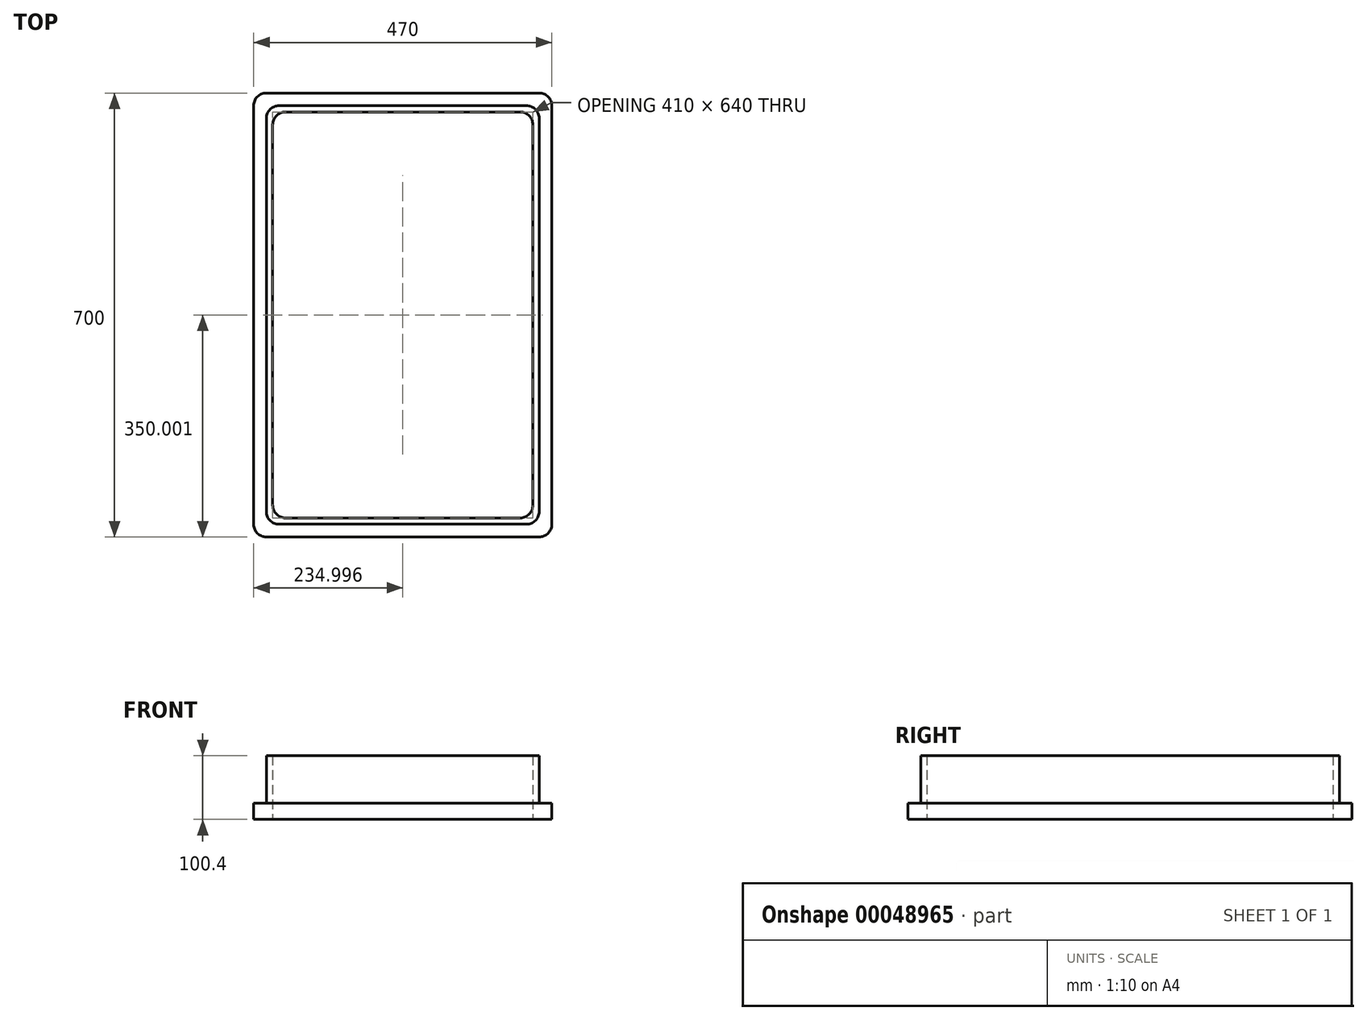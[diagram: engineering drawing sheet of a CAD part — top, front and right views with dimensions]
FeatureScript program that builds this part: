
annotation { "Feature Type Name" : "Feature", "Feature Type Description" : "" }
export const myFeature = defineFeature(function(context is Context, id is Id, definition is map)
    precondition{}
    {
        {
            var Q0;
            Q0=qCreatedBy(makeId("Top.planeOp"),FACE);
            var sketch = newSketch(context, id + "F0", { "sketchPlane" : qUnion([Q0])});
            skLineSegment(sketch, "E0.bottom", {"start": v(-206.8, 298.95) * mm, "end": v(163.2, 298.95) * mm});
            skLineSegment(sketch, "E0.top", {"start": v(-206.8, -341.05) * mm, "end": v(163.2, -341.05) * mm});
            skLineSegment(sketch, "E0.left", {"start": v(-226.8, 278.95) * mm, "end": v(-226.8, -321.05) * mm});
            skLineSegment(sketch, "E0.right", {"start": v(183.2, 278.95) * mm, "end": v(183.2, -321.05) * mm});
            skPoint(sketch, "E1.visualSharp", {"position": v(183.2, 298.95) * mm});
            skArc(sketch, "E1.filletArc", {"start": v(183.2, 278.95) * mm, "mid": v(177.35, 293.1) * mm, "end": v(163.2, 298.95) * mm});
            skPoint(sketch, "E2.visualSharp", {"position": v(-226.8, 298.95) * mm});
            skArc(sketch, "E2.filletArc", {"start": v(-206.8, 298.95) * mm, "mid": v(-220.94, 293.1) * mm, "end": v(-226.8, 278.95) * mm});
            skPoint(sketch, "E3.visualSharp", {"position": v(-226.8, -341.05) * mm});
            skArc(sketch, "E3.filletArc", {"start": v(-226.8, -321.05) * mm, "mid": v(-220.94, -335.2) * mm, "end": v(-206.8, -341.05) * mm});
            skPoint(sketch, "E4.visualSharp", {"position": v(183.2, -341.05) * mm});
            skArc(sketch, "E4.filletArc", {"start": v(163.2, -341.05) * mm, "mid": v(177.35, -335.2) * mm, "end": v(183.2, -321.05) * mm});
            skLineSegment(sketch, "E5.bottom", {"start": v(-216.8, 308.95) * mm, "end": v(173.2, 308.95) * mm});
            skLineSegment(sketch, "E5.top", {"start": v(-216.8, -351.05) * mm, "end": v(173.2, -351.05) * mm});
            skLineSegment(sketch, "E5.left", {"start": v(-236.8, 288.95) * mm, "end": v(-236.8, -331.05) * mm});
            skLineSegment(sketch, "E5.right", {"start": v(193.2, 288.95) * mm, "end": v(193.2, -331.05) * mm});
            skPoint(sketch, "E6.visualSharp", {"position": v(-236.8, -351.05) * mm});
            skArc(sketch, "E6.filletArc", {"start": v(-236.8, -331.05) * mm, "mid": v(-230.94, -345.2) * mm, "end": v(-216.8, -351.05) * mm});
            skPoint(sketch, "E7.visualSharp", {"position": v(-236.8, 308.95) * mm});
            skArc(sketch, "E7.filletArc", {"start": v(-216.8, 308.95) * mm, "mid": v(-230.94, 303.1) * mm, "end": v(-236.8, 288.95) * mm});
            skPoint(sketch, "E8.visualSharp", {"position": v(193.2, 308.95) * mm});
            skArc(sketch, "E8.filletArc", {"start": v(193.2, 288.95) * mm, "mid": v(187.35, 303.1) * mm, "end": v(173.2, 308.95) * mm});
            skPoint(sketch, "E9.visualSharp", {"position": v(193.2, -351.05) * mm});
            skArc(sketch, "E9.filletArc", {"start": v(173.2, -351.05) * mm, "mid": v(187.35, -345.2) * mm, "end": v(193.2, -331.05) * mm});
            skSolve(sketch);
        }
        {
            var Q0;
            Q0=makeQuery(id+"F0.imprint","IMPRINT",FACE,{"disambiguationData":[TD([[makeQuery(id+"F0.imprint","IMPRINT",EDGE,{"derivedFrom":sQuery(id+"F0.wireOp",EDGE,"E0.bottom")}),1.0]])]});
            extrude(context, id + "F1", {"entities" : qUnion([Q0]), "depth" : 75 * mm});
        }
        {
            var Q0;
            Q0=makeQuery(id+"F1.opExtrude","CAP_FACE",FACE,{"disambiguationData":[OSD([sQuery(id+"F0.wireOp",EDGE,"E0.bottom"),sQuery(id+"F0.wireOp",EDGE,"E0.top"),sQuery(id+"F0.wireOp",EDGE,"E0.left"),sQuery(id+"F0.wireOp",EDGE,"E0.right"),sQuery(id+"F0.wireOp",EDGE,"E1.filletArc"),sQuery(id+"F0.wireOp",EDGE,"E2.filletArc"),sQuery(id+"F0.wireOp",EDGE,"E3.filletArc"),sQuery(id+"F0.wireOp",EDGE,"E4.filletArc"),sQuery(id+"F0.wireOp",EDGE,"E5.bottom"),sQuery(id+"F0.wireOp",EDGE,"E5.top"),sQuery(id+"F0.wireOp",EDGE,"E5.left"),sQuery(id+"F0.wireOp",EDGE,"E5.right"),sQuery(id+"F0.wireOp",EDGE,"E6.filletArc"),sQuery(id+"F0.wireOp",EDGE,"E7.filletArc"),sQuery(id+"F0.wireOp",EDGE,"E8.filletArc"),sQuery(id+"F0.wireOp",EDGE,"E9.filletArc")])],"isStart":true});
            var sketch = newSketch(context, id + "F2", { "sketchPlane" : qUnion([Q0])});
            skLineSegment(sketch, "E10.bottom", {"start": v(-236.8, -328.95) * mm, "end": v(193.2, -328.95) * mm});
            skLineSegment(sketch, "E10.top", {"start": v(-236.8, 371.05) * mm, "end": v(193.2, 371.05) * mm});
            skLineSegment(sketch, "E10.left", {"start": v(-256.8, -308.95) * mm, "end": v(-256.8, 351.05) * mm});
            skLineSegment(sketch, "E10.right", {"start": v(213.2, -308.95) * mm, "end": v(213.2, 351.05) * mm});
            skPoint(sketch, "E11.visualSharp", {"position": v(-256.8, -328.95) * mm});
            skArc(sketch, "E11.filletArc", {"start": v(-256.8, -308.95) * mm, "mid": v(-250.94, -323.1) * mm, "end": v(-236.8, -328.95) * mm});
            skPoint(sketch, "E12.visualSharp", {"position": v(213.2, -328.95) * mm});
            skArc(sketch, "E12.filletArc", {"start": v(193.2, -328.95) * mm, "mid": v(207.35, -323.1) * mm, "end": v(213.2, -308.95) * mm});
            skPoint(sketch, "E13.visualSharp", {"position": v(213.2, 371.05) * mm});
            skArc(sketch, "E13.filletArc", {"start": v(213.2, 351.05) * mm, "mid": v(207.35, 365.2) * mm, "end": v(193.2, 371.05) * mm});
            skPoint(sketch, "E14.visualSharp", {"position": v(-256.8, 371.05) * mm});
            skArc(sketch, "E14.filletArc", {"start": v(-236.8, 371.05) * mm, "mid": v(-250.94, 365.2) * mm, "end": v(-256.8, 351.05) * mm});
            skLineSegment(sketch, "E15.bottom", {"start": v(-206.8, -298.95) * mm, "end": v(163.2, -298.95) * mm});
            skLineSegment(sketch, "E15.top", {"start": v(-206.8, 341.05) * mm, "end": v(163.2, 341.05) * mm});
            skLineSegment(sketch, "E15.left", {"start": v(-226.8, -278.95) * mm, "end": v(-226.8, 321.05) * mm});
            skLineSegment(sketch, "E15.right", {"start": v(183.2, -278.95) * mm, "end": v(183.2, 321.05) * mm});
            skPoint(sketch, "E16.visualSharp", {"position": v(-226.8, -298.95) * mm});
            skArc(sketch, "E16.filletArc", {"start": v(-226.8, -278.95) * mm, "mid": v(-220.94, -293.1) * mm, "end": v(-206.8, -298.95) * mm});
            skPoint(sketch, "E17.visualSharp", {"position": v(183.2, -298.95) * mm});
            skArc(sketch, "E17.filletArc", {"start": v(163.2, -298.95) * mm, "mid": v(177.35, -293.1) * mm, "end": v(183.2, -278.95) * mm});
            skPoint(sketch, "E18.visualSharp", {"position": v(183.2, 341.05) * mm});
            skArc(sketch, "E18.filletArc", {"start": v(183.2, 321.05) * mm, "mid": v(177.35, 335.2) * mm, "end": v(163.2, 341.05) * mm});
            skPoint(sketch, "E19.visualSharp", {"position": v(-226.8, 341.05) * mm});
            skArc(sketch, "E19.filletArc", {"start": v(-206.8, 341.05) * mm, "mid": v(-220.94, 335.2) * mm, "end": v(-226.8, 321.05) * mm});
            skSolve(sketch);
        }
        {
            var Q0;
            Q0=makeQuery(id+"F2.imprint","IMPRINT",FACE,{"disambiguationData":[TD([[makeQuery(id+"F2.imprint","IMPRINT",EDGE,{"derivedFrom":sQuery(id+"F2.wireOp",EDGE,"E10.bottom")}),1.0]])]});
            var Q1;
            Q1=makeQuery(id+"F2.imprint","IMPRINT",FACE,{"disambiguationData":[TD([[makeQuery(id+"F2.imprint","IMPRINT",EDGE,{"derivedFrom":sQuery(id+"F2.wireOp",EDGE,"E15.bottom")}),-1.0]])]});
            extrude(context, id + "F3", {"entities" : qUnion([Q0, Q1]), "operationType" : NewBodyOperationType.ADD, "depth" : 25.4 * mm});
        }
    });
